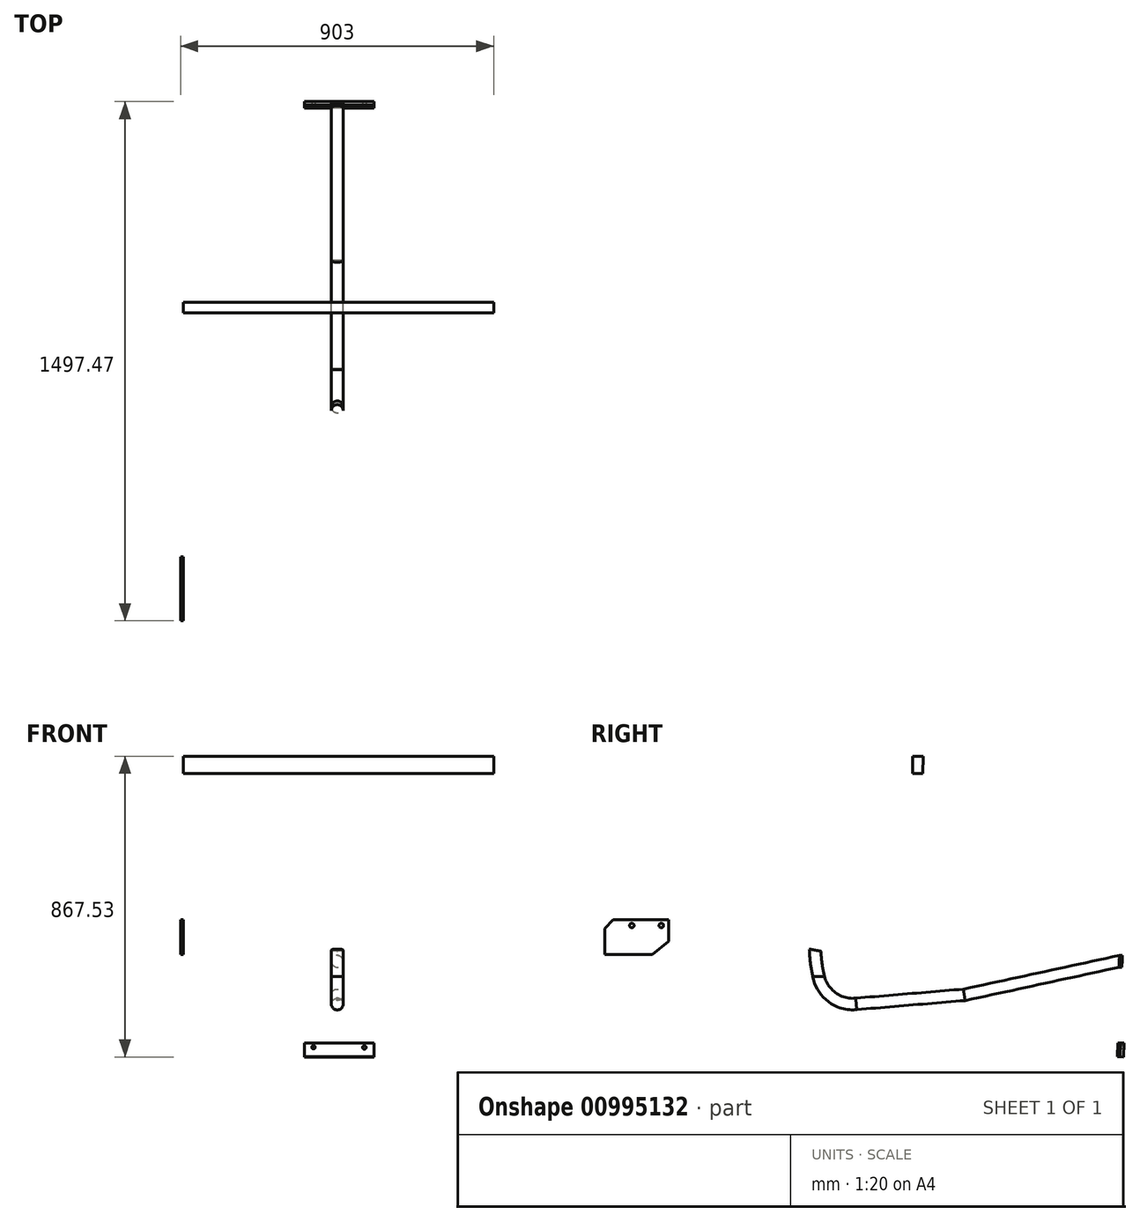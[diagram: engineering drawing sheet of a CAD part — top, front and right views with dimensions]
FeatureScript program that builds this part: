
annotation { "Feature Type Name" : "Feature", "Feature Type Description" : "" }
export const myFeature = defineFeature(function(context is Context, id is Id, definition is map)
    precondition{}
    {
        {
            var Q0;
            Q0=qCreatedBy(makeId("Right.planeOp"),FACE);
            var sketch = newSketch(context, id + "F0", { "sketchPlane" : qUnion([Q0])});
            skLineSegment(sketch, "E0", {"start": v(1.99, 17.58) * mm, "end": v(280.68, 44.64) * mm, "construction": true});
            skLineSegment(sketch, "E1.bottom", {"start": v(0, 0) * mm, "end": v(-179.15, 0) * mm, "construction": true});
            skLineSegment(sketch, "E1.top", {"start": v(0, -101.68) * mm, "end": v(-179.15, -101.68) * mm, "construction": true});
            skLineSegment(sketch, "E1.left", {"start": v(0, 0) * mm, "end": v(0, -101.68) * mm, "construction": true});
            skLineSegment(sketch, "E1.right", {"start": v(-179.15, 0) * mm, "end": v(-179.15, -101.68) * mm, "construction": true});
            skLineSegment(sketch, "E2", {"start": v(0, 0) * mm, "end": v(1.99, 34.94) * mm, "construction": true});
            skSolve(sketch);
        }
        {
            var Q0;
            Q0=qCreatedBy(makeId("Right.planeOp"),FACE);
            var sketch = newSketch(context, id + "F1", { "sketchPlane" : qUnion([Q0])});
            skLineSegment(sketch, "E3", {"start": v(0, 17) * mm, "end": v(310.92, 43) * mm});
            skArc(sketch, "E4", {"start": v(0, 17) * mm, "mid": v(-61.45, 33.28) * mm, "end": v(-96.96, 86.01) * mm});
            skArc(sketch, "E5", {"start": v(-96.96, 86.01) * mm, "mid": v(-103.9, 122.76) * mm, "end": v(-107.4, 160) * mm});
            skLineSegment(sketch, "E6", {"start": v(310.92, 43) * mm, "end": v(759.87, 140.04) * mm});
            skLineSegment(sketch, "E7", {"start": v(678.2, 122.38) * mm, "end": v(674.6, 139) * mm, "construction": true});
            skSolve(sketch);
        }
        {
            var Q0;
            Q0=qCreatedBy(makeId("Top.planeOp"),FACE);
            var Q1;
            Q1=sQuery(id+"F1.wireOp",VERTEX,"E5.end");
            cPlane(context, id + "F2", {"entities" : qUnion([Q0, Q1]), "cplaneType" : CPlaneType.PLANE_POINT, "offset" : 25 * mm, "width" : 150 * mm, "height" : 150 * mm});
        }
        {
            var Q0;
            Q0=qCreatedBy(id+"F2.planeOp",FACE);
            var sketch = newSketch(context, id + "F3", { "sketchPlane" : qUnion([Q0])});
            skCircle(sketch, "E8", {"center": v(0, -107.4) * mm, "radius": 17 * mm});
            skSolve(sketch);
        }
        {
            var Q0;
            Q0=makeQuery(id+"F3.imprint","IMPRINT",FACE,{"disambiguationData":[TD([[makeQuery(id+"F3.imprint","IMPRINT",EDGE,{"derivedFrom":sQuery(id+"F3.wireOp",EDGE,"E8")}),1.0]])]});
            var Q1;
            Q1=sQuery(id+"F1.wireOp",EDGE,"E5");
            var Q2;
            Q2=sQuery(id+"F1.wireOp",EDGE,"E4");
            var Q3;
            Q3=sQuery(id+"F1.wireOp",EDGE,"E3");
            var Q4;
            Q4=sQuery(id+"F1.wireOp",EDGE,"E6");
            sweep(context, id + "F4", {"profiles" : qUnion([Q0]), "path" : qUnion([Q1, Q2, Q3, Q4])});
        }
        {
            var Q0;
            Q0=makeQuery(id+"F4.opSweep","CAP_FACE",FACE,{"disambiguationData":[OSD([sQuery(id+"F1.wireOp",VERTEX,"E5.end"),sQuery(id+"F3.wireOp",EDGE,"E8")])],"isStart":true});
            var sketch = newSketch(context, id + "F5", { "sketchPlane" : qUnion([Q0])});
            skLineSegment(sketch, "E9.bottom", {"start": v(-106, -130.4) * mm, "end": v(94, -130.4) * mm});
            skLineSegment(sketch, "E9.top", {"start": v(-106, -90.4) * mm, "end": v(94, -90.4) * mm});
            skLineSegment(sketch, "E9.left", {"start": v(-106, -130.4) * mm, "end": v(-106, -90.4) * mm});
            skLineSegment(sketch, "E9.right", {"start": v(94, -130.4) * mm, "end": v(94, -90.4) * mm});
            skLineSegment(sketch, "E10", {"start": v(-6, -90.4) * mm, "end": v(-6, -130.4) * mm, "construction": true});
            skLineSegment(sketch, "E11", {"start": v(0, -124.4) * mm, "end": v(0, -90.4) * mm, "construction": true});
            skCircle(sketch, "E12", {"center": v(-77.9, -103.4) * mm, "radius": 5 * mm});
            skCircle(sketch, "E13", {"center": v(68.6, -102.6) * mm, "radius": 5 * mm});
            skSolve(sketch);
        }
        {
            var Q0;
            Q0=makeQuery(id+"F5.imprint","IMPRINT",FACE,{"disambiguationData":[TD([[makeQuery(id+"F5.imprint","IMPRINT",EDGE,{"derivedFrom":sQuery(id+"F5.wireOp",EDGE,"E9.bottom")}),1.0]])]});
            var Q1;
            Q1=makeQuery(id+"F5.imprint","IMPRINT",FACE,{"disambiguationData":[TD([[makeQuery(id+"F5.imprint","IMPRINT",EDGE,{"derivedFrom":makeQuery(id+"F4.opSweep","CAP_EDGE",EDGE,{"disambiguationData":[OSD([sQuery(id+"F1.wireOp",VERTEX,"E5.end"),sQuery(id+"F3.wireOp",EDGE,"E8")])],"isStart":true})}),-1.0]])]});
            extrude(context, id + "F6", {"entities" : qUnion([Q0, Q1]), "operationType" : NewBodyOperationType.ADD, "depth" : 8 * mm, "offsetDistance" : 25 * mm});
        }
        {
            var Q0;
            Q0=makeQuery(id+"F6.opExtrude","SWEPT_FACE",FACE,{"disambiguationData":[OSD([sQuery(id+"F5.wireOp",EDGE,"E9.top")])]});
            cPlane(context, id + "F7", {"entities" : qUnion([Q0]), "cplaneType" : CPlaneType.OFFSET, "offset" : 765 * mm, "width" : 150 * mm, "height" : 150 * mm});
        }
        {
            var Q0;
            Q0=qCreatedBy(id+"F7.planeOp",FACE);
            var sketch = newSketch(context, id + "F8", { "sketchPlane" : qUnion([Q0])});
            skLineSegment(sketch, "E14.bottom", {"start": v(451, 179.5) * mm, "end": v(-444, 179.5) * mm});
            skLineSegment(sketch, "E14.top", {"start": v(451, 149.5) * mm, "end": v(-444, 149.5) * mm});
            skLineSegment(sketch, "E14.left", {"start": v(451, 179.5) * mm, "end": v(451, 149.5) * mm});
            skLineSegment(sketch, "E14.right", {"start": v(-444, 179.5) * mm, "end": v(-444, 149.5) * mm});
            skLineSegment(sketch, "E15", {"start": v(0, 149.5) * mm, "end": v(0, 139) * mm, "construction": true});
            skSolve(sketch);
        }
        {
            var Q0;
            Q0=makeQuery(id+"F8.imprint","IMPRINT",FACE,{"disambiguationData":[TD([[makeQuery(id+"F8.imprint","IMPRINT",EDGE,{"derivedFrom":sQuery(id+"F8.wireOp",EDGE,"E14.bottom")}),1.0]])]});
            extrude(context, id + "F9", {"entities" : qUnion([Q0]), "operationType" : NewBodyOperationType.ADD, "depth" : 50 * mm, "offsetDistance" : 25 * mm});
        }
        {
            var Q0;
            Q0=makeQuery(id+"F9.opExtrude","SWEPT_FACE",FACE,{"disambiguationData":[OSD([sQuery(id+"F8.wireOp",EDGE,"E14.right")])]});
            var sketch = newSketch(context, id + "F10", { "sketchPlane" : qUnion([Q0])});
            skLineSegment(sketch, "E16", {"start": v(724.6, 149.5) * mm, "end": v(587.6, 149.5) * mm});
            skLineSegment(sketch, "E17", {"start": v(587.6, 149.5) * mm, "end": v(539.6, 187.5) * mm});
            skLineSegment(sketch, "E18", {"start": v(539.6, 187.5) * mm, "end": v(539.6, 249.5) * mm});
            skLineSegment(sketch, "E19", {"start": v(539.6, 249.5) * mm, "end": v(699.6, 249.5) * mm});
            skLineSegment(sketch, "E20", {"start": v(699.6, 249.5) * mm, "end": v(724.6, 224.5) * mm});
            skLineSegment(sketch, "E21", {"start": v(724.6, 224.5) * mm, "end": v(724.6, 149.5) * mm});
            skCircle(sketch, "E22", {"center": v(561.1, 233) * mm, "radius": 6.5 * mm});
            skCircle(sketch, "E23", {"center": v(646.1, 233) * mm, "radius": 6.5 * mm});
            skSolve(sketch);
        }
        {
            var Q0;
            Q0 = qSketchRegion(id + "F10", true);
            extrude(context, id + "F11", {"entities" : qUnion([Q0]), "operationType" : NewBodyOperationType.ADD, "depth" : 8 * mm, "offsetDistance" : 25 * mm});
        }
        {
            var Q0;
            Q0=makeQuery(id+"F6.opExtrude","CAP_FACE",FACE,{"disambiguationData":[OSD([sQuery(id+"F5.wireOp",EDGE,"E9.bottom"),sQuery(id+"F5.wireOp",EDGE,"E9.top"),sQuery(id+"F5.wireOp",EDGE,"E9.left"),sQuery(id+"F5.wireOp",EDGE,"E9.right"),sQuery(id+"F5.wireOp",EDGE,"E12"),sQuery(id+"F5.wireOp",EDGE,"E13")])],"isStart":false});
            extrude(context, id + "F12", {"entities" : qUnion([Q0]), "depth" : 10 * mm, "offsetDistance" : 25 * mm});
        }
    });
